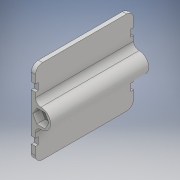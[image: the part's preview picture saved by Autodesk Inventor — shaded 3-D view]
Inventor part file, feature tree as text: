
AUTODESK INVENTOR PART (.ipt)
format: ipt  version: 2019 (Build 230136000, 136)  size: 165,376 bytes
history: native  units: mm
features: extrude x3, sketch x3, other x1, fillet x1
ambient origin geometry x8: Origin, YZ Plane, XZ Plane, XY Plane, X Axis, Y Axis, Z Axis, Center Point
bodies: Body1 (feature_tree)
feature tree (8):
  other  "Sólido1"
  extrude  "Extrusión1"  Depth=10.2mm
  extrude  "Extrusión2"  Depth=3.0mm
  extrude  "Extrusión3"  Depth=10.0mm
  fillet  "Empalme1"  Radius=6.0mm
  sketch  "Boceto1"  dims[d0=6.3mm d3=10.2mm]
  sketch  "Boceto2"  dims[d4=1.0mm d5=3.0mm]
  sketch  "Boceto4"  dims[d6=70.0mm d7=0.0mm d8=10.0mm d9=6.0mm d10=0.0mm d12=60.0mm d16=6.0mm d17=0.0mm d18=5.0mm d19=5.0mm d20=2.0mm]
